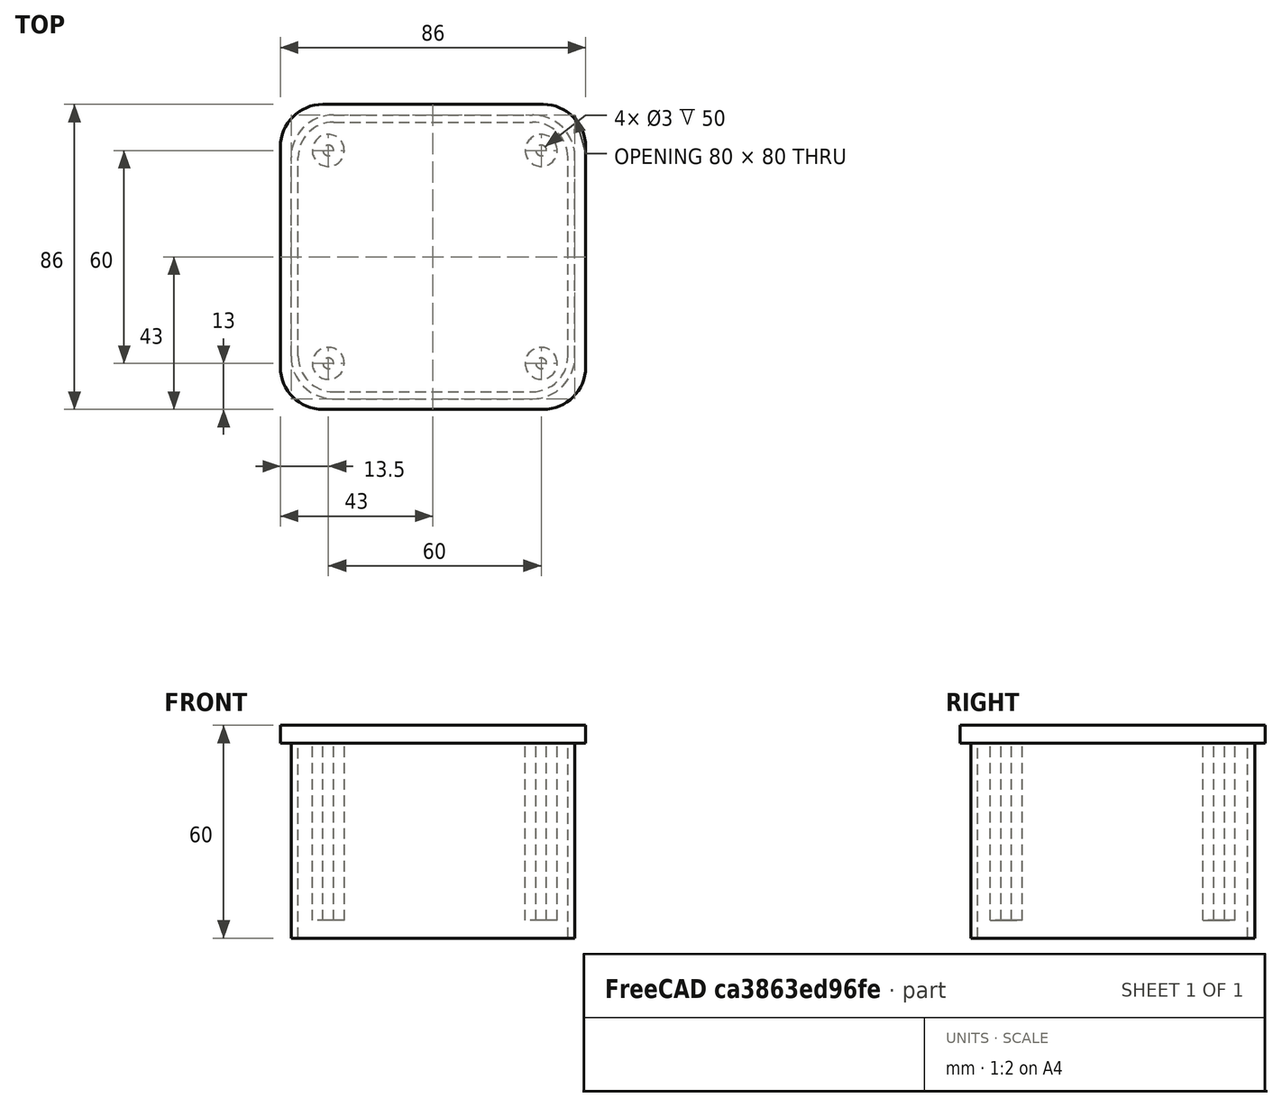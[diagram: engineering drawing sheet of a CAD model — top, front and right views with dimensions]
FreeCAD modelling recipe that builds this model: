
FCSTD DOCUMENT  (FreeCAD 0.17R13522 (Git))
Label: JoselitoBOX_V2_1withoutholes
License: All rights reserved
LicenseURL: http://en.wikipedia.org/wiki/All_rights_reserved
objects: Part::Cylinder×6, Part::Cut×4, Part::MultiFuse×3, Part::Box×2, Part::Fillet×2, Part::Thickness×1
note: 18 computed .brp shape members not serialized (recipe doc carries the construction recipe); baked Part::Feature solids carry a one-line shape summary decoded from their .brp

FEATURE [Part::Box] Box  label="Cubo"
  AttacherType = Attacher::AttachEngine3D
  Height = 60
  Length = 80
  Width = 80
FEATURE [Part::Fillet] Fillet001
  Base = -> Box
  Edges = 4 edges r=12: [Edge1,Edge3,Edge5,Edge7]
FEATURE [Part::Thickness] Thickness001  label="CAJA"
  Faces = -> Fillet001 [Face5]
  Intersection = false
  Join = 0
  Mode = 0
  Placement = pos=(2,2,4) rot=(0,0,1;0rad)
  SelfIntersection = false
  Value = -2
FEATURE [Part::Cut] Cut001
  Placement = pos=(5.5,5,6) rot=(0,0,1;0rad)
FEATURE [Part::Cylinder] Cylinder002  label="Cilindro002"
  Angle = 360
  AttacherType = Attacher::AttachEngine3D
  Height = 63
  Placement = pos=(7,7,3) rot=(0,0,1;0rad)
  Radius = 1.5
FEATURE [Part::Cylinder] Cylinder003  label="Cilindro003"
  Angle = 360
  AttacherType = Attacher::AttachEngine3D
  Height = 55
  Placement = pos=(7,7,3) rot=(0,0,1;0rad)
  Radius = 4.5
FEATURE [Part::Cut] Cut002
  Base = -> Cylinder003
  Placement = pos=(5.5,65,6) rot=(0,0,1;0rad)
  Tool = -> Cylinder002
FEATURE [Part::Cylinder] Cylinder004  label="Cilindro004"
  Angle = 360
  AttacherType = Attacher::AttachEngine3D
  Height = 63
  Placement = pos=(7,7,3) rot=(0,0,1;0rad)
  Radius = 1.5
FEATURE [Part::Cylinder] Cylinder005  label="Cilindro005"
  Angle = 360
  AttacherType = Attacher::AttachEngine3D
  Height = 55
  Placement = pos=(7,7,3) rot=(0,0,1;0rad)
  Radius = 4.5
FEATURE [Part::Cut] Cut003
  Base = -> Cylinder005
  Placement = pos=(65.5,65,6) rot=(0,0,1;0rad)
  Tool = -> Cylinder004
FEATURE [Part::Cylinder] Cylinder006  label="Cilindro006"
  Angle = 360
  AttacherType = Attacher::AttachEngine3D
  Height = 63
  Placement = pos=(7,7,3) rot=(0,0,1;0rad)
  Radius = 1.5
FEATURE [Part::Cylinder] Cylinder007  label="Cilindro007"
  Angle = 360
  AttacherType = Attacher::AttachEngine3D
  Height = 55
  Placement = pos=(7,7,3) rot=(0,0,1;0rad)
  Radius = 4.5
FEATURE [Part::Cut] Cut004
  Base = -> Cylinder007
  Placement = pos=(65.5,5,6) rot=(0,0,1;0rad)
  Tool = -> Cylinder006
FEATURE [Part::MultiFuse] Fusion  label="cilindros"
  Shapes = -> [Cut001,Cut003,Cut004,Cut002]
FEATURE [Part::Box] Box012  label="Cubo005"
  AttacherType = Attacher::AttachEngine3D
  Height = 5
  Length = 86
  Width = 86
FEATURE [Part::Fillet] Fillet004
  Base = -> Box012
  Edges = 4 edges r=12: [Edge1,Edge3,Edge5,Edge7]
  Placement = pos=(-1,-1,59) rot=(0,0,1;0rad)
FEATURE [Part::MultiFuse] Fusion004
  Shapes = -> [Fusion,Thickness001]
FEATURE [Part::MultiFuse] Fusion005  label="CajasinHuecos"
  Shapes = -> [Fusion004,Fillet004]
